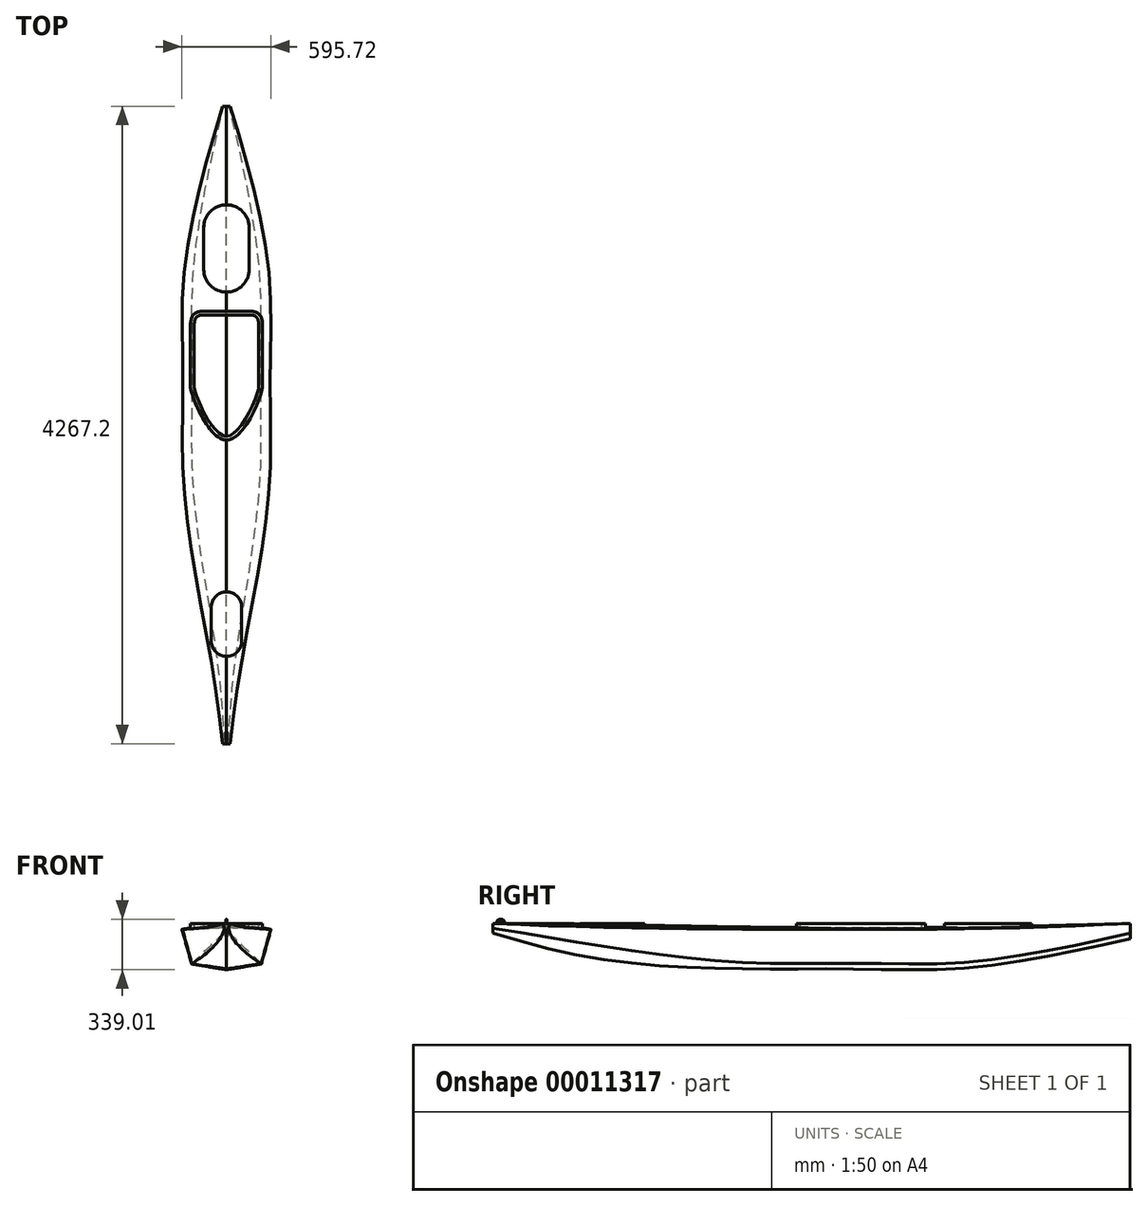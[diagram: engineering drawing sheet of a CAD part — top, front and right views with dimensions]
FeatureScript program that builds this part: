
annotation { "Feature Type Name" : "Feature", "Feature Type Description" : "" }
export const myFeature = defineFeature(function(context is Context, id is Id, definition is map)
    precondition{}
    {
        {
            var Q0;
            Q0=qCreatedBy(makeId("Front.planeOp"),FACE);
            var sketch = newSketch(context, id + "F0", { "sketchPlane" : qUnion([Q0])});
            skLineSegment(sketch, "E0", {"start": v(0, 0) * mm, "end": v(25.4, 0) * mm});
            skLineSegment(sketch, "E1", {"start": v(25.4, 0) * mm, "end": v(12.7, -31.75) * mm});
            skLineSegment(sketch, "E2.0.MirrorCS", {"start": v(0, 0) * mm, "end": v(-25.4, 0) * mm});
            skLineSegment(sketch, "E3.0.MirrorCS", {"start": v(-25.4, 0) * mm, "end": v(-12.7, -31.75) * mm});
            skPoint(sketch, "E4", {"position": v(12.7, -31.75) * mm});
            skPoint(sketch, "E5.0.MirrorP", {"position": v(-12.7, -31.75) * mm});
            skLineSegment(sketch, "E6", {"start": v(12.7, -31.75) * mm, "end": v(0, -63.5) * mm});
            skLineSegment(sketch, "E7", {"start": v(-12.7, -31.75) * mm, "end": v(0, -63.5) * mm});
            skSolve(sketch);
        }
        {
            var Q0;
            Q0=qCreatedBy(makeId("Front.planeOp"),FACE);
            cPlane(context, id + "F1", {"entities" : qUnion([Q0]), "cplaneType" : CPlaneType.OFFSET, "offset" : 304.8 * mm, "oppositeDirection" : true, "width" : 152.4 * mm, "height" : 152.4 * mm});
        }
        {
            var Q0;
            Q0=qCreatedBy(id+"F1.planeOp",FACE);
            var sketch = newSketch(context, id + "F2", { "sketchPlane" : qUnion([Q0])});
            skLineSegment(sketch, "E8", {"start": v(0, 0) * mm, "end": v(63.5, -12.7) * mm});
            skLineSegment(sketch, "E9", {"start": v(63.5, -12.7) * mm, "end": v(31.75, -82.55) * mm});
            skLineSegment(sketch, "E10.0.MirrorCS", {"start": v(0, 0) * mm, "end": v(-63.5, -12.7) * mm});
            skLineSegment(sketch, "E11.0.MirrorCS", {"start": v(-63.5, -12.7) * mm, "end": v(-31.75, -82.55) * mm});
            skPoint(sketch, "E12", {"position": v(31.75, -82.55) * mm});
            skPoint(sketch, "E13.0.MirrorP", {"position": v(-31.75, -82.55) * mm});
            skLineSegment(sketch, "E14", {"start": v(31.75, -82.55) * mm, "end": v(0, -152.4) * mm});
            skLineSegment(sketch, "E15", {"start": v(-31.75, -82.55) * mm, "end": v(0, -152.4) * mm});
            skSolve(sketch);
        }
        {
            var Q0;
            Q0=qCreatedBy(id+"F1.planeOp",FACE);
            cPlane(context, id + "F3", {"entities" : qUnion([Q0]), "cplaneType" : CPlaneType.OFFSET, "offset" : 304.8 * mm, "oppositeDirection" : true, "width" : 152.4 * mm, "height" : 152.4 * mm});
        }
        {
            var Q0;
            Q0=qCreatedBy(id+"F3.planeOp",FACE);
            var sketch = newSketch(context, id + "F4", { "sketchPlane" : qUnion([Q0])});
            skLineSegment(sketch, "E16", {"start": v(0, 0) * mm, "end": v(228.6, -25.4) * mm});
            skLineSegment(sketch, "E17", {"start": v(228.6, -25.4) * mm, "end": v(152.4, -152.4) * mm});
            skLineSegment(sketch, "E18", {"start": v(152.4, -152.4) * mm, "end": v(0, -203.2) * mm});
            skLineSegment(sketch, "E19.0.MirrorCS", {"start": v(0, 0) * mm, "end": v(-228.6, -25.4) * mm});
            skLineSegment(sketch, "E20.0.MirrorCS", {"start": v(-228.6, -25.4) * mm, "end": v(-152.4, -152.4) * mm});
            skLineSegment(sketch, "E21.0.MirrorCS", {"start": v(-152.4, -152.4) * mm, "end": v(0, -203.2) * mm});
            skSolve(sketch);
        }
        {
            var Q0;
            Q0=qCreatedBy(id+"F3.planeOp",FACE);
            cPlane(context, id + "F5", {"entities" : qUnion([Q0]), "cplaneType" : CPlaneType.OFFSET, "offset" : 304.8 * mm, "oppositeDirection" : true, "width" : 152.4 * mm, "height" : 152.4 * mm});
        }
        {
            var Q0;
            Q0=qCreatedBy(id+"F5.planeOp",FACE);
            var sketch = newSketch(context, id + "F6", { "sketchPlane" : qUnion([Q0])});
            skLineSegment(sketch, "E22", {"start": v(0, 0) * mm, "end": v(254, -31.75) * mm});
            skLineSegment(sketch, "E23", {"start": v(254, -31.75) * mm, "end": v(190.5, -190.5) * mm});
            skLineSegment(sketch, "E24", {"start": v(190.5, -190.5) * mm, "end": v(0, -241.3) * mm});
            skLineSegment(sketch, "E25.0.MirrorCS", {"start": v(0, 0) * mm, "end": v(-254, -31.75) * mm});
            skLineSegment(sketch, "E26.0.MirrorCS", {"start": v(-254, -31.75) * mm, "end": v(-190.5, -190.5) * mm});
            skLineSegment(sketch, "E27.0.MirrorCS", {"start": v(-190.5, -190.5) * mm, "end": v(0, -241.3) * mm});
            skSolve(sketch);
        }
        {
            var Q0;
            Q0=qCreatedBy(id+"F5.planeOp",FACE);
            cPlane(context, id + "F7", {"entities" : qUnion([Q0]), "cplaneType" : CPlaneType.OFFSET, "offset" : 304.8 * mm, "oppositeDirection" : true, "width" : 152.4 * mm, "height" : 152.4 * mm});
        }
        {
            var Q0;
            Q0=qCreatedBy(id+"F7.planeOp",FACE);
            var sketch = newSketch(context, id + "F8", { "sketchPlane" : qUnion([Q0])});
            skLineSegment(sketch, "E28", {"start": v(0, -12.7) * mm, "end": v(279.4, -38.1) * mm});
            skLineSegment(sketch, "E29", {"start": v(279.4, -38.1) * mm, "end": v(228.6, -203.2) * mm});
            skLineSegment(sketch, "E30", {"start": v(228.6, -203.2) * mm, "end": v(0, -266.7) * mm});
            skLineSegment(sketch, "E31.0.MirrorCS", {"start": v(0, -12.7) * mm, "end": v(-279.4, -38.1) * mm});
            skLineSegment(sketch, "E32.0.MirrorCS", {"start": v(-279.4, -38.1) * mm, "end": v(-228.6, -203.2) * mm});
            skLineSegment(sketch, "E33.0.MirrorCS", {"start": v(-228.6, -203.2) * mm, "end": v(0, -266.7) * mm});
            skSolve(sketch);
        }
        {
            var Q0;
            Q0=qCreatedBy(id+"F7.planeOp",FACE);
            cPlane(context, id + "F9", {"entities" : qUnion([Q0]), "cplaneType" : CPlaneType.OFFSET, "offset" : 304.8 * mm, "oppositeDirection" : true, "width" : 152.4 * mm, "height" : 152.4 * mm});
        }
        {
            var Q0;
            Q0=qCreatedBy(id+"F9.planeOp",FACE);
            var sketch = newSketch(context, id + "F10", { "sketchPlane" : qUnion([Q0])});
            skLineSegment(sketch, "E34", {"start": v(0, -25.4) * mm, "end": v(292.1, -38.1) * mm});
            skLineSegment(sketch, "E35", {"start": v(292.1, -38.1) * mm, "end": v(228.6, -228.6) * mm});
            skLineSegment(sketch, "E36", {"start": v(228.6, -228.6) * mm, "end": v(0, -292.1) * mm});
            skLineSegment(sketch, "E37.0.MirrorCS", {"start": v(0, -25.4) * mm, "end": v(-292.1, -38.1) * mm});
            skLineSegment(sketch, "E38.0.MirrorCS", {"start": v(-292.1, -38.1) * mm, "end": v(-228.6, -228.6) * mm});
            skLineSegment(sketch, "E39.0.MirrorCS", {"start": v(-228.6, -228.6) * mm, "end": v(0, -292.1) * mm});
            skSolve(sketch);
        }
        {
            var Q0;
            Q0=qCreatedBy(id+"F9.planeOp",FACE);
            cPlane(context, id + "F11", {"entities" : qUnion([Q0]), "cplaneType" : CPlaneType.OFFSET, "offset" : 304.8 * mm, "oppositeDirection" : true, "width" : 152.4 * mm, "height" : 152.4 * mm});
        }
        {
            var Q0;
            Q0=qCreatedBy(id+"F11.planeOp",FACE);
            var sketch = newSketch(context, id + "F12", { "sketchPlane" : qUnion([Q0])});
            skLineSegment(sketch, "E40", {"start": v(0, -25.4) * mm, "end": v(292.1, -38.1) * mm});
            skLineSegment(sketch, "E41", {"start": v(292.1, -38.1) * mm, "end": v(228.6, -266.7) * mm});
            skLineSegment(sketch, "E42", {"start": v(228.6, -266.7) * mm, "end": v(0, -304.8) * mm});
            skLineSegment(sketch, "E43.0.MirrorCS", {"start": v(0, -25.4) * mm, "end": v(-292.1, -38.1) * mm});
            skLineSegment(sketch, "E44.0.MirrorCS", {"start": v(-292.1, -38.1) * mm, "end": v(-228.6, -266.7) * mm});
            skLineSegment(sketch, "E45.0.MirrorCS", {"start": v(-228.6, -266.7) * mm, "end": v(0, -304.8) * mm});
            skSolve(sketch);
        }
        {
            var Q0;
            Q0=qCreatedBy(id+"F11.planeOp",FACE);
            cPlane(context, id + "F13", {"entities" : qUnion([Q0]), "cplaneType" : CPlaneType.OFFSET, "offset" : 304.8 * mm, "oppositeDirection" : true, "width" : 152.4 * mm, "height" : 152.4 * mm});
        }
        {
            var Q0;
            Q0=qCreatedBy(id+"F13.planeOp",FACE);
            var sketch = newSketch(context, id + "F14", { "sketchPlane" : qUnion([Q0])});
            skLineSegment(sketch, "E46.0.0", {"start": v(292.1, -38.1) * mm, "end": v(0, -25.4) * mm});
            skLineSegment(sketch, "E46.0.1", {"start": v(0, -25.4) * mm, "end": v(-292.1, -38.1) * mm});
            skLineSegment(sketch, "E46.0.2", {"start": v(-292.1, -38.1) * mm, "end": v(-228.6, -266.7) * mm});
            skLineSegment(sketch, "E46.0.3", {"start": v(-228.6, -266.7) * mm, "end": v(0, -304.8) * mm});
            skLineSegment(sketch, "E46.0.4", {"start": v(0, -304.8) * mm, "end": v(228.6, -266.7) * mm});
            skLineSegment(sketch, "E46.0.5", {"start": v(228.6, -266.7) * mm, "end": v(292.1, -38.1) * mm});
            skSolve(sketch);
        }
        {
            var Q0;
            Q0=qCreatedBy(id+"F13.planeOp",FACE);
            cPlane(context, id + "F15", {"entities" : qUnion([Q0]), "cplaneType" : CPlaneType.OFFSET, "offset" : 304.8 * mm, "oppositeDirection" : true, "width" : 152.4 * mm, "height" : 152.4 * mm});
        }
        {
            var Q0;
            Q0=qCreatedBy(id+"F15.planeOp",FACE);
            var sketch = newSketch(context, id + "F16", { "sketchPlane" : qUnion([Q0])});
            skLineSegment(sketch, "E47.0.0", {"start": v(228.6, -266.7) * mm, "end": v(292.1, -38.1) * mm});
            skLineSegment(sketch, "E47.0.1", {"start": v(292.1, -38.1) * mm, "end": v(0, -25.4) * mm});
            skLineSegment(sketch, "E47.0.2", {"start": v(0, -25.4) * mm, "end": v(-292.1, -38.1) * mm});
            skLineSegment(sketch, "E47.0.3", {"start": v(-292.1, -38.1) * mm, "end": v(-228.6, -266.7) * mm});
            skLineSegment(sketch, "E47.0.4", {"start": v(-228.6, -266.7) * mm, "end": v(0, -304.8) * mm});
            skLineSegment(sketch, "E47.0.5", {"start": v(0, -304.8) * mm, "end": v(228.6, -266.7) * mm});
            skSolve(sketch);
        }
        {
            var Q0;
            Q0=qCreatedBy(id+"F15.planeOp",FACE);
            cPlane(context, id + "F17", {"entities" : qUnion([Q0]), "cplaneType" : CPlaneType.OFFSET, "offset" : 304.8 * mm, "oppositeDirection" : true, "width" : 152.4 * mm, "height" : 152.4 * mm});
        }
        {
            var Q0;
            Q0=qCreatedBy(id+"F17.planeOp",FACE);
            var sketch = newSketch(context, id + "F18", { "sketchPlane" : qUnion([Q0])});
            skLineSegment(sketch, "E48.0.0", {"start": v(0, -304.8) * mm, "end": v(228.6, -266.7) * mm});
            skLineSegment(sketch, "E48.0.1", {"start": v(228.6, -266.7) * mm, "end": v(292.1, -38.1) * mm});
            skLineSegment(sketch, "E48.0.2", {"start": v(292.1, -38.1) * mm, "end": v(0, -25.4) * mm});
            skLineSegment(sketch, "E48.0.3", {"start": v(0, -25.4) * mm, "end": v(-292.1, -38.1) * mm});
            skLineSegment(sketch, "E48.0.4", {"start": v(-292.1, -38.1) * mm, "end": v(-228.6, -266.7) * mm});
            skLineSegment(sketch, "E48.0.5", {"start": v(-228.6, -266.7) * mm, "end": v(0, -304.8) * mm});
            skSolve(sketch);
        }
        {
            var Q0;
            Q0=qCreatedBy(id+"F17.planeOp",FACE);
            cPlane(context, id + "F19", {"entities" : qUnion([Q0]), "cplaneType" : CPlaneType.OFFSET, "offset" : 304.8 * mm, "oppositeDirection" : true, "width" : 152.4 * mm, "height" : 152.4 * mm});
        }
        {
            var Q0;
            Q0=qCreatedBy(id+"F19.planeOp",FACE);
            var sketch = newSketch(context, id + "F20", { "sketchPlane" : qUnion([Q0])});
            skLineSegment(sketch, "E49.0.0", {"start": v(-228.6, -266.7) * mm, "end": v(0, -304.8) * mm});
            skLineSegment(sketch, "E49.0.1", {"start": v(0, -304.8) * mm, "end": v(228.6, -266.7) * mm});
            skLineSegment(sketch, "E49.0.2", {"start": v(228.6, -266.7) * mm, "end": v(292.1, -38.1) * mm});
            skLineSegment(sketch, "E49.0.3", {"start": v(292.1, -38.1) * mm, "end": v(0, -25.4) * mm});
            skLineSegment(sketch, "E49.0.4", {"start": v(0, -25.4) * mm, "end": v(-292.1, -38.1) * mm});
            skLineSegment(sketch, "E49.0.5", {"start": v(-292.1, -38.1) * mm, "end": v(-228.6, -266.7) * mm});
            skSolve(sketch);
        }
        {
            var Q0;
            Q0=qCreatedBy(id+"F19.planeOp",FACE);
            cPlane(context, id + "F21", {"entities" : qUnion([Q0]), "cplaneType" : CPlaneType.OFFSET, "offset" : 1219.2 * mm, "oppositeDirection" : true, "width" : 152.4 * mm, "height" : 152.4 * mm});
        }
        {
            var Q0;
            Q0=qCreatedBy(id+"F21.planeOp",FACE);
            var sketch = newSketch(context, id + "F22", { "sketchPlane" : qUnion([Q0])});
            skLineSegment(sketch, "E50", {"start": v(0, 0) * mm, "end": v(25.4, 0) * mm});
            skLineSegment(sketch, "E51", {"start": v(25.4, 0) * mm, "end": v(19.05, -63.5) * mm});
            skLineSegment(sketch, "E52", {"start": v(19.05, -63.5) * mm, "end": v(0, -101.6) * mm});
            skLineSegment(sketch, "E53.0.MirrorCS", {"start": v(0, 0) * mm, "end": v(-25.4, 0) * mm});
            skLineSegment(sketch, "E54.0.MirrorCS", {"start": v(-25.4, 0) * mm, "end": v(-19.05, -63.5) * mm});
            skLineSegment(sketch, "E55.0.MirrorCS", {"start": v(-19.05, -63.5) * mm, "end": v(0, -101.6) * mm});
            skSolve(sketch);
        }
        {
            var Q0;
            Q0=makeQuery(id+"F0.imprint","IMPRINT",FACE,{"disambiguationData":[TD([[makeQuery(id+"F0.imprint","IMPRINT",EDGE,{"derivedFrom":sQuery(id+"F0.wireOp",EDGE,"E0")}),-1.0]])]});
            var Q1;
            Q1=makeQuery(id+"F2.imprint","IMPRINT",FACE,{"disambiguationData":[TD([[makeQuery(id+"F2.imprint","IMPRINT",EDGE,{"derivedFrom":sQuery(id+"F2.wireOp",EDGE,"E8")}),-1.0]])]});
            var Q2;
            Q2=makeQuery(id+"F12.imprint","IMPRINT",FACE,{"disambiguationData":[TD([[makeQuery(id+"F12.imprint","IMPRINT",EDGE,{"derivedFrom":sQuery(id+"F12.wireOp",EDGE,"E40")}),-1.0]])]});
            var Q3;
            Q3=makeQuery(id+"F16.imprint","IMPRINT",FACE,{"disambiguationData":[TD([[makeQuery(id+"F16.imprint","IMPRINT",EDGE,{"derivedFrom":sQuery(id+"F16.wireOp",EDGE,"E47.0.0")}),1.0]])]});
            var Q4;
            Q4=makeQuery(id+"F20.imprint","IMPRINT",FACE,{"disambiguationData":[TD([[makeQuery(id+"F20.imprint","IMPRINT",EDGE,{"derivedFrom":sQuery(id+"F20.wireOp",EDGE,"E49.0.0")}),1.0]])]});
            var Q5;
            Q5=makeQuery(id+"F22.imprint","IMPRINT",FACE,{"disambiguationData":[TD([[makeQuery(id+"F22.imprint","IMPRINT",EDGE,{"derivedFrom":sQuery(id+"F22.wireOp",EDGE,"E50")}),-1.0]])]});
            loft(context, id + "F23", {"sheetProfilesArray" : [{ "sheetProfileEntities" : qUnion([Q0]) }, { "sheetProfileEntities" : qUnion([Q1]) }, { "sheetProfileEntities" : qUnion([Q2]) }, { "sheetProfileEntities" : qUnion([Q3]) }, { "sheetProfileEntities" : qUnion([Q4]) }, { "sheetProfileEntities" : qUnion([Q5]) }]});
        }
        {
            var Q0;
            Q0=qCreatedBy(makeId("Right.planeOp"),FACE);
            var sketch = newSketch(context, id + "F24", { "sketchPlane" : qUnion([Q0])});
            skArc(sketch, "E56", {"start": v(76.2, 0) * mm, "mid": v(50.8, 25.94) * mm, "end": v(25.4, 0) * mm});
            skSolve(sketch);
        }
        {
            var Q0;
            Q0=qCreatedBy(makeId("Top.planeOp"),FACE);
            var sketch = newSketch(context, id + "F25", { "sketchPlane" : qUnion([Q0])});
            skPoint(sketch, "E57.0", {"position": v(0, 25.4) * mm});
            skCircle(sketch, "E58", {"center": v(0, 25.4) * mm, "radius": 3.18 * mm});
            skSolve(sketch);
        }
        {
            var Q0;
            Q0 = qSketchRegion(id + "F25", true);
            var Q1;
            Q1=sQuery(id+"F24.wireOp",EDGE,"E56");
            sweep(context, id + "F26", {"operationType" : NewBodyOperationType.ADD, "profiles" : qUnion([Q0]), "path" : qUnion([Q1])});
        }
        {
            var Q0;
            Q0=qCreatedBy(makeId("Top.planeOp"),FACE);
            var sketch = newSketch(context, id + "F27", { "sketchPlane" : qUnion([Q0])});
            skLineSegment(sketch, "E59", {"start": v(0, 2895.6) * mm, "end": v(139.7, 2895.6) * mm});
            skLineSegment(sketch, "E60", {"start": v(241.3, 2794) * mm, "end": v(241.3, 2387.6) * mm});
            skPoint(sketch, "E61", {"position": v(241.3, 2387.6) * mm});
            skFitSpline(sketch, "E62", {"points": [v(139.7, 2895.6) * mm, v(241.3, 2794) * mm], "startDerivative": vector(228.6, 0) * mm, "endDerivative": vector(0, -228.6) * mm});
            skFitSpline(sketch, "E63", {"points": [v(241.3, 2387.6) * mm, v(0, 2032) * mm, v(-241.3, 2387.6) * mm], "startDerivative": vector(0, -304.8) * mm, "endDerivative": vector(0, 304.8) * mm});
            skLineSegment(sketch, "E64.0.MirrorCS", {"start": v(0, 2895.6) * mm, "end": v(-139.7, 2895.6) * mm});
            skFitSpline(sketch, "E65.0.MirrorCS", {"points": [v(-139.7, 2895.6) * mm, v(-241.3, 2794) * mm], "startDerivative": vector(-228.6, 0) * mm, "endDerivative": vector(0, -228.6) * mm});
            skLineSegment(sketch, "E66.0.MirrorCS", {"start": v(-241.3, 2794) * mm, "end": v(-241.3, 2387.6) * mm});
            skLineSegment(sketch, "E67.0", {"start": v(0, 2870.2) * mm, "end": v(-139.7, 2870.2) * mm});
            skLineSegment(sketch, "E67.1", {"start": v(0, 2870.2) * mm, "end": v(139.7, 2870.2) * mm});
            skFitSpline(sketch, "E67.2", {"points": [v(139.7, 2870.2) * mm, v(144.1, 2870.2) * mm, v(152.45, 2870.02) * mm, v(163.52, 2869.19) * mm, v(173.13, 2867.83) * mm, v(181.28, 2866) * mm, v(188, 2863.78) * mm, v(193.4, 2861.26) * mm, v(197.7, 2858.51) * mm, v(201.2, 2855.5) * mm, v(204.21, 2852) * mm, v(206.96, 2847.7) * mm, v(209.48, 2842.3) * mm, v(211.7, 2835.58) * mm, v(213.53, 2827.43) * mm, v(214.89, 2817.82) * mm, v(215.72, 2806.75) * mm, v(215.9, 2798.4) * mm, v(215.9, 2794) * mm]});
            skLineSegment(sketch, "E67.3", {"start": v(215.9, 2794) * mm, "end": v(215.9, 2387.6) * mm});
            skFitSpline(sketch, "E67.4", {"points": [v(215.9, 2387.6) * mm, v(215.9, 2387.43) * mm, v(215.88, 2386.78) * mm, v(215.73, 2385.04) * mm, v(215.43, 2382.7) * mm, v(214.8, 2378.9) * mm, v(213.58, 2373.03) * mm, v(211.45, 2364.52) * mm, v(208.69, 2354.76) * mm, v(204.18, 2340.3) * mm, v(197.1, 2319.87) * mm, v(186.46, 2292.58) * mm, v(173.9, 2263.39) * mm, v(159.63, 2233.19) * mm, v(143.84, 2202.84) * mm, v(126.75, 2173.2) * mm, v(108.6, 2145.15) * mm, v(89.68, 2119.56) * mm, v(73.53, 2101.04) * mm, v(60.62, 2088.33) * mm, v(51.02, 2079.96) * mm, v(41.58, 2072.85) * mm, v(32.4, 2067.05) * mm, v(25.06, 2063.36) * mm, v(19.41, 2061.1) * mm, v(15.3, 2059.72) * mm, v(11.3, 2058.67) * mm, v(7.44, 2057.93) * mm, v(4.3, 2057.57) * mm, v(1.83, 2057.42) * mm, v(0, 2057.39) * mm, v(-1.83, 2057.42) * mm, v(-4.3, 2057.57) * mm, v(-7.44, 2057.93) * mm, v(-11.3, 2058.67) * mm, v(-15.3, 2059.72) * mm, v(-19.41, 2061.1) * mm, v(-25.06, 2063.36) * mm, v(-32.4, 2067.05) * mm, v(-41.58, 2072.85) * mm, v(-51.02, 2079.96) * mm, v(-60.62, 2088.33) * mm, v(-73.53, 2101.04) * mm, v(-89.68, 2119.56) * mm, v(-108.6, 2145.15) * mm, v(-126.75, 2173.2) * mm, v(-143.84, 2202.84) * mm, v(-159.63, 2233.19) * mm, v(-173.9, 2263.39) * mm, v(-186.46, 2292.58) * mm, v(-197.1, 2319.87) * mm, v(-204.18, 2340.3) * mm, v(-208.69, 2354.76) * mm, v(-211.45, 2364.52) * mm, v(-213.58, 2373.03) * mm, v(-214.8, 2378.9) * mm, v(-215.43, 2382.7) * mm, v(-215.73, 2385.04) * mm, v(-215.88, 2386.78) * mm, v(-215.9, 2387.43) * mm, v(-215.9, 2387.6) * mm]});
            skFitSpline(sketch, "E67.5", {"points": [v(-139.7, 2870.2) * mm, v(-144.1, 2870.2) * mm, v(-152.45, 2870.02) * mm, v(-163.52, 2869.19) * mm, v(-173.13, 2867.83) * mm, v(-181.28, 2866) * mm, v(-188, 2863.78) * mm, v(-193.4, 2861.26) * mm, v(-197.7, 2858.51) * mm, v(-201.2, 2855.5) * mm, v(-204.21, 2852) * mm, v(-206.96, 2847.7) * mm, v(-209.48, 2842.3) * mm, v(-211.7, 2835.58) * mm, v(-213.53, 2827.43) * mm, v(-214.89, 2817.82) * mm, v(-215.72, 2806.75) * mm, v(-215.9, 2798.4) * mm, v(-215.9, 2794) * mm]});
            skLineSegment(sketch, "E67.6", {"start": v(-215.9, 2794) * mm, "end": v(-215.9, 2387.6) * mm});
            skFitSpline(sketch, "E68.0", {"points": [v(0, 3048) * mm, v(0, 3454.4) * mm, v(0, 3860.8) * mm, v(0, 4267.2) * mm], "construction": true});
            skArc(sketch, "E69", {"start": v(-152.4, 3175) * mm, "mid": v(-107.76, 3067.24) * mm, "end": v(0, 3022.6) * mm});
            skArc(sketch, "E70", {"start": v(0, 3606.8) * mm, "mid": v(-107.76, 3562.16) * mm, "end": v(-152.4, 3454.4) * mm});
            skLineSegment(sketch, "E71", {"start": v(-152.4, 3175) * mm, "end": v(-152.4, 3454.4) * mm});
            skArc(sketch, "E72.0.MirrorCS", {"start": v(152.4, 3175) * mm, "mid": v(107.76, 3067.24) * mm, "end": v(0, 3022.6) * mm});
            skLineSegment(sketch, "E73.0.MirrorCS", {"start": v(152.4, 3175) * mm, "end": v(152.4, 3454.4) * mm});
            skArc(sketch, "E74.0.MirrorCS", {"start": v(0, 3606.8) * mm, "mid": v(107.76, 3562.16) * mm, "end": v(152.4, 3454.4) * mm});
            skArc(sketch, "E75", {"start": v(-101.6, 685.8) * mm, "mid": v(-71.84, 613.96) * mm, "end": v(0, 584.2) * mm});
            skLineSegment(sketch, "E76", {"start": v(-101.6, 685.8) * mm, "end": v(-101.6, 914.4) * mm});
            skArc(sketch, "E77", {"start": v(0, 1016) * mm, "mid": v(-71.84, 986.24) * mm, "end": v(-101.6, 914.4) * mm});
            skArc(sketch, "E78.0.MirrorCS", {"start": v(101.6, 685.8) * mm, "mid": v(71.84, 613.96) * mm, "end": v(0, 584.2) * mm});
            skLineSegment(sketch, "E79.0.MirrorCS", {"start": v(101.6, 685.8) * mm, "end": v(101.6, 914.4) * mm});
            skArc(sketch, "E80.0.MirrorCS", {"start": v(0, 1016) * mm, "mid": v(71.84, 986.24) * mm, "end": v(101.6, 914.4) * mm});
            skSolve(sketch);
        }
        {
            var Q0;
            Q0 = qSketchRegion(id + "F27", true);
            var Q1;
            Q1=makeQuery(id+"F23.opLoft","SWEPT_FACE",FACE,{"disambiguationData":[OSD([sQuery(id+"F0.wireOp",EDGE,"E0"),sQuery(id+"F0.wireOp",EDGE,"E1"),sQuery(id+"F0.wireOp",EDGE,"E2.0.MirrorCS"),sQuery(id+"F2.wireOp",EDGE,"E8"),sQuery(id+"F2.wireOp",EDGE,"E9"),sQuery(id+"F2.wireOp",EDGE,"E10.0.MirrorCS")])]});
            extrude(context, id + "F28", {"entities" : qUnion([Q0]), "operationType" : NewBodyOperationType.ADD, "endBound" : BoundingType.UP_TO_BODY, "oppositeDirection" : true, "endBoundEntityBody" : qUnion([Q1]), "depth" : 25.4 * mm});
        }
    });
